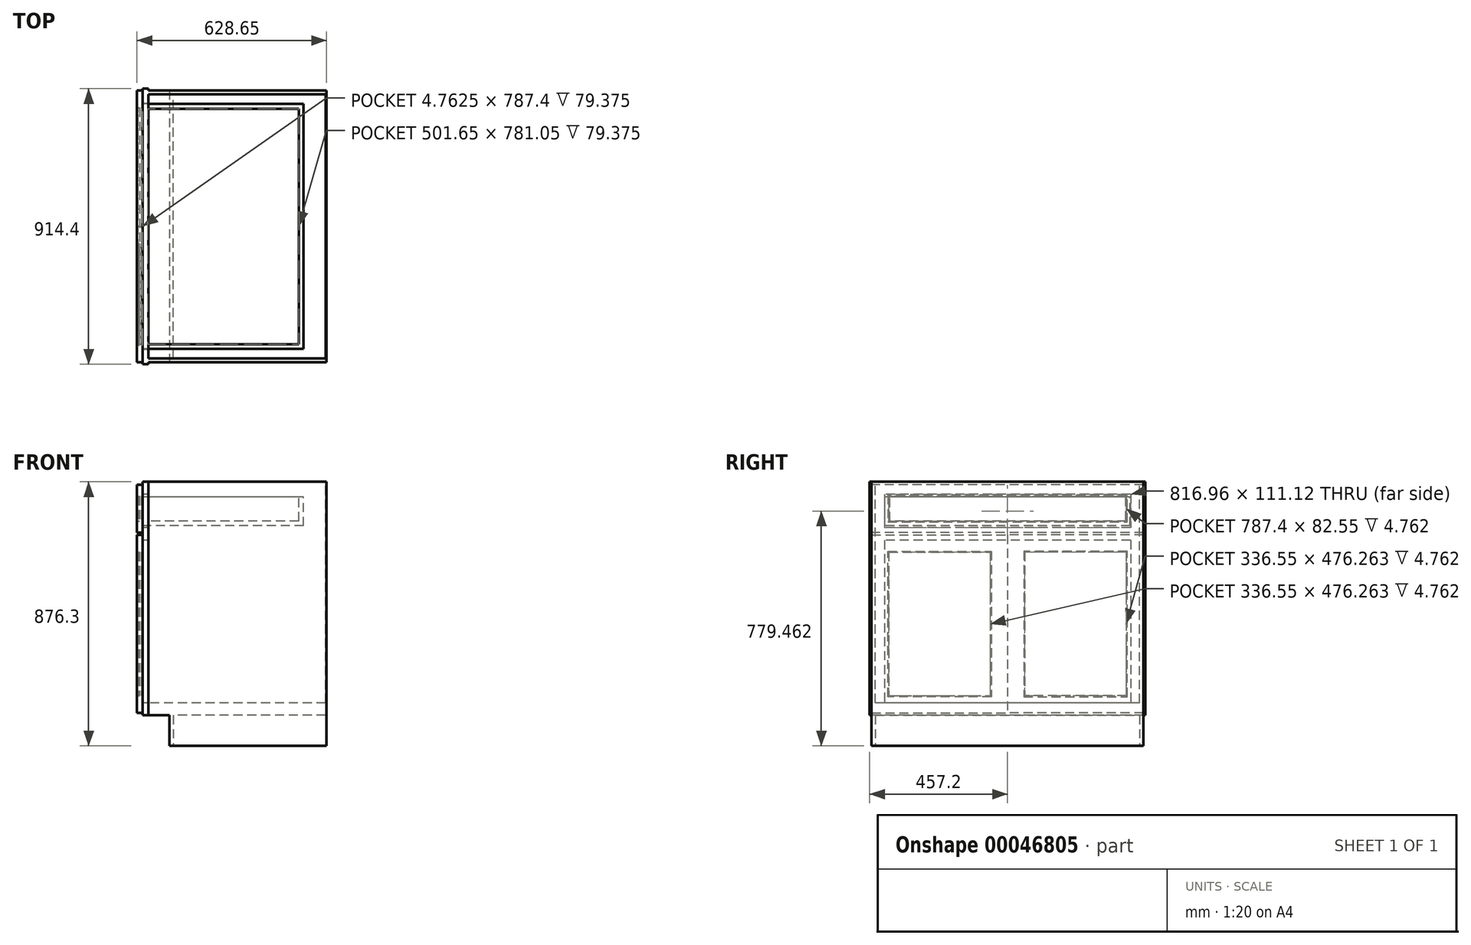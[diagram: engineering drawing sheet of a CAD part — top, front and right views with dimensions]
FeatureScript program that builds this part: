
annotation { "Feature Type Name" : "Feature", "Feature Type Description" : "" }
export const myFeature = defineFeature(function(context is Context, id is Id, definition is map)
    precondition{}
    {
        {
            var Q0;
            Q0=qCreatedBy(makeId("Front.planeOp"),FACE);
            var sketch = newSketch(context, id + "F0", { "sketchPlane" : qUnion([Q0])});
            skLineSegment(sketch, "E0.bottom", {"start": v(-304.8, -438.15) * mm, "end": v(304.8, -438.15) * mm});
            skLineSegment(sketch, "E0.top", {"start": v(-304.8, 438.15) * mm, "end": v(304.8, 438.15) * mm});
            skLineSegment(sketch, "E0.left", {"start": v(-304.8, -438.15) * mm, "end": v(-304.8, 438.15) * mm});
            skLineSegment(sketch, "E0.right", {"start": v(304.8, -438.15) * mm, "end": v(304.8, 438.15) * mm});
            skLineSegment(sketch, "E1", {"start": v(-304.8, -438.15) * mm, "end": v(304.8, 438.15) * mm, "construction": true});
            skSolve(sketch);
        }
        {
            var Q0;
            Q0=qSketchRegion(id+"F0",true);
            extrude(context, id + "F1", {"entities" : qUnion([Q0]), "oppositeDirection" : true, "depth" : 914.4 * mm});
        }
        {
            var Q0;
            Q0=makeQuery(id+"F1.opExtrude","CAP_FACE",FACE,{"disambiguationData":[OSD([sQuery(id+"F0.wireOp",EDGE,"E0.bottom"),sQuery(id+"F0.wireOp",EDGE,"E0.top"),sQuery(id+"F0.wireOp",EDGE,"E0.left"),sQuery(id+"F0.wireOp",EDGE,"E0.right")])],"isStart":true});
            var sketch = newSketch(context, id + "F2", { "sketchPlane" : qUnion([Q0])});
            skLineSegment(sketch, "E2.bottom", {"start": v(-304.8, -438.15) * mm, "end": v(-215.9, -438.15) * mm});
            skLineSegment(sketch, "E2.top", {"start": v(-304.8, -336.55) * mm, "end": v(-215.9, -336.55) * mm});
            skLineSegment(sketch, "E2.left", {"start": v(-304.8, -438.15) * mm, "end": v(-304.8, -336.55) * mm});
            skLineSegment(sketch, "E2.right", {"start": v(-215.9, -438.15) * mm, "end": v(-215.9, -336.55) * mm});
            skSolve(sketch);
        }
        {
            var Q0;
            Q0=qSketchRegion(id+"F2",true);
            extrude(context, id + "F3", {"entities" : qUnion([Q0]), "operationType" : NewBodyOperationType.REMOVE, "endBound" : BoundingType.THROUGH_ALL, "oppositeDirection" : true, "depth" : 25.4 * mm});
        }
        {
            var Q0;
            Q0=makeQuery(id+"F1.opExtrude","SWEPT_FACE",FACE,{"disambiguationData":[OSD([sQuery(id+"F0.wireOp",EDGE,"E0.left")])]});
            var sketch = newSketch(context, id + "F4", { "sketchPlane" : qUnion([Q0])});
            skLineSegment(sketch, "E3.bottom", {"start": v(-865.68, 396.88) * mm, "end": v(-48.72, 396.88) * mm});
            skLineSegment(sketch, "E3.top", {"start": v(-865.68, -295.28) * mm, "end": v(-48.72, -295.28) * mm});
            skLineSegment(sketch, "E3.left", {"start": v(-865.68, 396.88) * mm, "end": v(-865.68, -295.28) * mm});
            skLineSegment(sketch, "E3.right", {"start": v(-48.72, 396.88) * mm, "end": v(-48.72, -295.28) * mm});
            skLineSegment(sketch, "E4", {"start": v(-914.4, 438.15) * mm, "end": v(0, -336.55) * mm, "construction": true});
            skSolve(sketch);
        }
        {
            var Q0;
            Q0=qSketchRegion(id+"F4",true);
            extrude(context, id + "F5", {"entities" : qUnion([Q0]), "operationType" : NewBodyOperationType.REMOVE, "oppositeDirection" : true, "depth" : 19.05 * mm});
        }
        {
            var Q0;
            Q0=makeQuery(id+"F1.opExtrude","SWEPT_FACE",FACE,{"disambiguationData":[OSD([sQuery(id+"F0.wireOp",EDGE,"E0.top")])]});
            var sketch = newSketch(context, id + "F6", { "sketchPlane" : qUnion([Q0])});
            skLineSegment(sketch, "E5.bottom", {"start": v(304.8, 914.4) * mm, "end": v(-285.75, 914.4) * mm});
            skLineSegment(sketch, "E5.top", {"start": v(304.8, 908.05) * mm, "end": v(-285.75, 908.05) * mm});
            skLineSegment(sketch, "E5.left", {"start": v(304.8, 914.4) * mm, "end": v(304.8, 908.05) * mm});
            skLineSegment(sketch, "E5.right", {"start": v(-285.75, 914.4) * mm, "end": v(-285.75, 908.05) * mm});
            skLineSegment(sketch, "E6.bottom", {"start": v(304.8, 0) * mm, "end": v(-285.75, 0) * mm});
            skLineSegment(sketch, "E6.top", {"start": v(304.8, 6.35) * mm, "end": v(-285.75, 6.35) * mm});
            skLineSegment(sketch, "E6.left", {"start": v(304.8, 0) * mm, "end": v(304.8, 6.35) * mm});
            skLineSegment(sketch, "E6.right", {"start": v(-285.75, 0) * mm, "end": v(-285.75, 6.35) * mm});
            skSolve(sketch);
        }
        {
            var Q0;
            Q0=qSketchRegion(id+"F6",true);
            extrude(context, id + "F7", {"entities" : qUnion([Q0]), "operationType" : NewBodyOperationType.REMOVE, "endBound" : BoundingType.THROUGH_ALL, "oppositeDirection" : true, "depth" : 25.4 * mm});
        }
        {
            var Q0;
            Q0=makeQuery(id+"F1.opExtrude","SWEPT_FACE",FACE,{"disambiguationData":[OSD([sQuery(id+"F0.wireOp",EDGE,"E0.top")])]});
            var sketch = newSketch(context, id + "F8", { "sketchPlane" : qUnion([Q0])});
            skLineSegment(sketch, "E7.bottom", {"start": v(301.62, 895.35) * mm, "end": v(-285.75, 895.35) * mm});
            skLineSegment(sketch, "E7.top", {"start": v(301.63, 19.05) * mm, "end": v(-285.75, 19.05) * mm});
            skLineSegment(sketch, "E7.left", {"start": v(301.62, 895.35) * mm, "end": v(301.63, 19.05) * mm});
            skLineSegment(sketch, "E7.right", {"start": v(-285.75, 895.35) * mm, "end": v(-285.75, 19.05) * mm});
            skSolve(sketch);
        }
        {
            var Q0;
            Q0=qSketchRegion(id+"F8",true);
            var Q1;
            Q1=makeQuery(id+"F5.boolean.opBoolean","COPY",FACE,{"derivedFrom":makeQuery(id+"F5.opExtrude","SWEPT_FACE",FACE,{"disambiguationData":[OSD([sQuery(id+"F4.wireOp",EDGE,"E3.top")])]})});
            extrude(context, id + "F9", {"entities" : qUnion([Q0]), "operationType" : NewBodyOperationType.REMOVE, "endBound" : BoundingType.UP_TO_SURFACE, "oppositeDirection" : true, "endBoundEntityFace" : qUnion([Q1]), "depth" : 25.4 * mm});
        }
        {
            var Q0;
            Q0=makeQuery(id+"F1.opExtrude","SWEPT_FACE",FACE,{"disambiguationData":[OSD([sQuery(id+"F0.wireOp",EDGE,"E0.left")])]});
            var sketch = newSketch(context, id + "F10", { "sketchPlane" : qUnion([Q0])});
            skLineSegment(sketch, "E8.bottom", {"start": v(-865.68, 285.75) * mm, "end": v(-48.72, 285.75) * mm});
            skLineSegment(sketch, "E8.top", {"start": v(-865.68, 244.47) * mm, "end": v(-48.72, 244.47) * mm});
            skLineSegment(sketch, "E8.left", {"start": v(-865.68, 285.75) * mm, "end": v(-865.68, 244.47) * mm});
            skLineSegment(sketch, "E8.right", {"start": v(-48.72, 285.75) * mm, "end": v(-48.72, 244.47) * mm});
            skSolve(sketch);
        }
        {
            var Q0;
            Q0=qSketchRegion(id+"F10",true);
            var Q1;
            Q1=makeQuery(id+"F9.boolean.opBoolean","COPY",FACE,{"derivedFrom":makeQuery(id+"F9.opExtrude","SWEPT_FACE",FACE,{"disambiguationData":[OSD([sQuery(id+"F8.wireOp",EDGE,"E7.right")])]})});
            extrude(context, id + "F11", {"entities" : qUnion([Q0]), "operationType" : NewBodyOperationType.ADD, "endBound" : BoundingType.UP_TO_SURFACE, "oppositeDirection" : true, "endBoundEntityFace" : qUnion([Q1]), "depth" : 25.4 * mm});
        }
        {
            var Q0;
            Q0=makeQuery(id+"F11.boolean.opBoolean","MERGE",FACE,{"derivedFrom":[makeQuery(id+"F1.opExtrude","SWEPT_FACE",FACE,{"disambiguationData":[OSD([sQuery(id+"F0.wireOp",EDGE,"E0.left")])]}),makeQuery(id+"F11.opExtrude","CAP_FACE",FACE,{"disambiguationData":[OSD([sQuery(id+"F10.wireOp",EDGE,"E8.bottom"),sQuery(id+"F10.wireOp",EDGE,"E8.top"),sQuery(id+"F10.wireOp",EDGE,"E8.left"),sQuery(id+"F10.wireOp",EDGE,"E8.right")])],"isStart":true})]});
            var sketch = newSketch(context, id + "F12", { "sketchPlane" : qUnion([Q0])});
            skLineSegment(sketch, "E9.bottom", {"start": v(-908.05, 261.95) * mm, "end": v(-457.2, 261.95) * mm});
            skLineSegment(sketch, "E9.top", {"start": v(-908.05, -328.61) * mm, "end": v(-457.2, -328.61) * mm});
            skLineSegment(sketch, "E9.left", {"start": v(-908.05, 261.95) * mm, "end": v(-908.05, -328.61) * mm});
            skLineSegment(sketch, "E9.right", {"start": v(-457.2, 261.95) * mm, "end": v(-457.2, -328.61) * mm});
            skLineSegment(sketch, "E10.bottom", {"start": v(-850.9, 204.8) * mm, "end": v(-514.35, 204.8) * mm});
            skLineSegment(sketch, "E10.top", {"start": v(-850.9, -271.46) * mm, "end": v(-514.35, -271.46) * mm});
            skLineSegment(sketch, "E10.left", {"start": v(-850.9, 204.8) * mm, "end": v(-850.9, -271.46) * mm});
            skLineSegment(sketch, "E10.right", {"start": v(-514.35, 204.8) * mm, "end": v(-514.35, -271.46) * mm});
            skLineSegment(sketch, "E11", {"start": v(-457.2, 244.47) * mm, "end": v(-457.2, -295.28) * mm, "construction": true});
            skSolve(sketch);
        }
        {
            var Q0;
            Q0=qSketchRegion(id+"F12",true);
            extrude(context, id + "F13", {"entities" : qUnion([Q0]), "depth" : 19.05 * mm});
        }
        {
            var Q0;
            Q0=makeQuery(id+"F13.opExtrude","SWEPT_FACE",FACE,{"disambiguationData":[OSD([sQuery(id+"F12.wireOp",EDGE,"E10.top")])]});
            var sketch = newSketch(context, id + "F14", { "sketchPlane" : qUnion([Q0])});
            skLineSegment(sketch, "E12.bottom", {"start": v(-315.91, 850.9) * mm, "end": v(-309.56, 850.9) * mm});
            skLineSegment(sketch, "E12.top", {"start": v(-315.91, 514.35) * mm, "end": v(-309.56, 514.35) * mm});
            skLineSegment(sketch, "E12.left", {"start": v(-315.91, 850.9) * mm, "end": v(-315.91, 514.35) * mm});
            skLineSegment(sketch, "E12.right", {"start": v(-309.56, 850.9) * mm, "end": v(-309.56, 514.35) * mm});
            skSolve(sketch);
        }
        {
            var Q0;
            Q0=qSketchRegion(id+"F14",true);
            extrude(context, id + "F15", {"entities" : qUnion([Q0]), "operationType" : NewBodyOperationType.ADD, "endBound" : BoundingType.UP_TO_NEXT, "depth" : 25.4 * mm});
        }
        {
            var Q0;
            Q0=makeQuery(id+"F13.opExtrude","CAP_EDGE",EDGE,{"disambiguationData":[OSD([sQuery(id+"F12.wireOp",EDGE,"E10.left")])],"isStart":false});
            var Q1;
            Q1=makeQuery(id+"F13.opExtrude","CAP_EDGE",EDGE,{"disambiguationData":[OSD([sQuery(id+"F12.wireOp",EDGE,"E10.top")])],"isStart":false});
            var Q2;
            Q2=makeQuery(id+"F13.opExtrude","CAP_EDGE",EDGE,{"disambiguationData":[OSD([sQuery(id+"F12.wireOp",EDGE,"E10.right")])],"isStart":false});
            var Q3;
            Q3=makeQuery(id+"F13.opExtrude","CAP_EDGE",EDGE,{"disambiguationData":[OSD([sQuery(id+"F12.wireOp",EDGE,"E10.bottom")])],"isStart":false});
            chamfer(context, id + "F16", {"entities" : qUnion([Q0, Q1, Q2, Q3]), "width" : 3.17 * mm, "tangentPropagation" : true});
        }
        {
            var Q0;
            Q0=makeQuery(id+"F11.boolean.opBoolean","MERGE",FACE,{"derivedFrom":[makeQuery(id+"F1.opExtrude","SWEPT_FACE",FACE,{"disambiguationData":[OSD([sQuery(id+"F0.wireOp",EDGE,"E0.left")])]}),makeQuery(id+"F11.opExtrude","CAP_FACE",FACE,{"disambiguationData":[OSD([sQuery(id+"F10.wireOp",EDGE,"E8.bottom"),sQuery(id+"F10.wireOp",EDGE,"E8.top"),sQuery(id+"F10.wireOp",EDGE,"E8.left"),sQuery(id+"F10.wireOp",EDGE,"E8.right")])],"isStart":true})]});
            var sketch = newSketch(context, id + "F17", { "sketchPlane" : qUnion([Q0])});
            skLineSegment(sketch, "E13.bottom", {"start": v(-908.05, 428.62) * mm, "end": v(-6.35, 428.62) * mm});
            skLineSegment(sketch, "E13.top", {"start": v(-908.05, 269.88) * mm, "end": v(-6.35, 269.88) * mm});
            skLineSegment(sketch, "E13.left", {"start": v(-908.05, 428.62) * mm, "end": v(-908.05, 269.88) * mm});
            skLineSegment(sketch, "E13.right", {"start": v(-6.35, 428.63) * mm, "end": v(-6.35, 269.88) * mm});
            skLineSegment(sketch, "E14.bottom", {"start": v(-850.9, 390.52) * mm, "end": v(-63.5, 390.52) * mm});
            skLineSegment(sketch, "E14.top", {"start": v(-850.9, 307.98) * mm, "end": v(-63.5, 307.98) * mm});
            skLineSegment(sketch, "E14.left", {"start": v(-850.9, 390.52) * mm, "end": v(-850.9, 307.98) * mm});
            skLineSegment(sketch, "E14.right", {"start": v(-63.5, 390.53) * mm, "end": v(-63.5, 307.98) * mm});
            skSolve(sketch);
        }
        {
            var Q0;
            Q0=qSketchRegion(id+"F17",true);
            extrude(context, id + "F18", {"entities" : qUnion([Q0]), "depth" : 19.05 * mm});
        }
        {
            var Q0;
            Q0=makeQuery(id+"F18.opExtrude","SWEPT_FACE",FACE,{"disambiguationData":[OSD([sQuery(id+"F17.wireOp",EDGE,"E14.top")])]});
            var sketch = newSketch(context, id + "F19", { "sketchPlane" : qUnion([Q0])});
            skLineSegment(sketch, "E15.bottom", {"start": v(-309.56, 850.9) * mm, "end": v(-315.91, 850.9) * mm});
            skLineSegment(sketch, "E15.top", {"start": v(-309.56, 63.5) * mm, "end": v(-315.91, 63.5) * mm});
            skLineSegment(sketch, "E15.left", {"start": v(-309.56, 850.9) * mm, "end": v(-309.56, 63.5) * mm});
            skLineSegment(sketch, "E15.right", {"start": v(-315.91, 850.9) * mm, "end": v(-315.91, 63.5) * mm});
            skSolve(sketch);
        }
        {
            var Q0;
            Q0=qSketchRegion(id+"F19",true);
            var Q1;
            Q1=makeQuery(id+"F18.opExtrude","SWEPT_FACE",FACE,{"disambiguationData":[OSD([sQuery(id+"F17.wireOp",EDGE,"E14.bottom")])]});
            extrude(context, id + "F20", {"entities" : qUnion([Q0]), "operationType" : NewBodyOperationType.ADD, "endBound" : BoundingType.UP_TO_SURFACE, "endBoundEntityFace" : qUnion([Q1]), "depth" : 25.4 * mm});
        }
        {
            var Q0;
            Q0=makeQuery(id+"F18.opExtrude","CAP_EDGE",EDGE,{"disambiguationData":[OSD([sQuery(id+"F17.wireOp",EDGE,"E14.top")])],"isStart":false});
            var Q1;
            Q1=makeQuery(id+"F18.opExtrude","CAP_EDGE",EDGE,{"disambiguationData":[OSD([sQuery(id+"F17.wireOp",EDGE,"E14.left")])],"isStart":false});
            var Q2;
            Q2=makeQuery(id+"F18.opExtrude","CAP_EDGE",EDGE,{"disambiguationData":[OSD([sQuery(id+"F17.wireOp",EDGE,"E14.bottom")])],"isStart":false});
            var Q3;
            Q3=makeQuery(id+"F18.opExtrude","CAP_EDGE",EDGE,{"disambiguationData":[OSD([sQuery(id+"F17.wireOp",EDGE,"E14.right")])],"isStart":false});
            chamfer(context, id + "F21", {"entities" : qUnion([Q0, Q1, Q2, Q3]), "width" : 3.17 * mm, "tangentPropagation" : true});
        }
        {
            var Q0;
            Q0=makeQuery(id+"F1.opExtrude","SWEPT_FACE",FACE,{"disambiguationData":[OSD([sQuery(id+"F0.wireOp",EDGE,"E0.bottom")])]});
            var sketch = newSketch(context, id + "F22", { "sketchPlane" : qUnion([Q0])});
            skLineSegment(sketch, "E16.bottom", {"start": v(301.63, -19.05) * mm, "end": v(-203.2, -19.05) * mm});
            skLineSegment(sketch, "E16.top", {"start": v(301.63, -895.35) * mm, "end": v(-203.2, -895.35) * mm});
            skLineSegment(sketch, "E16.left", {"start": v(301.63, -19.05) * mm, "end": v(301.63, -895.35) * mm});
            skLineSegment(sketch, "E16.right", {"start": v(-203.2, -19.05) * mm, "end": v(-203.2, -895.35) * mm});
            skSolve(sketch);
        }
        {
            var Q0;
            Q0=qSketchRegion(id+"F22",true);
            extrude(context, id + "F23", {"entities" : qUnion([Q0]), "operationType" : NewBodyOperationType.REMOVE, "oppositeDirection" : true, "depth" : 101.6 * mm});
        }
        {
            var Q0;
            Q0=makeQuery(id+"F18.opExtrude","CAP_FACE",FACE,{"disambiguationData":[OSD([sQuery(id+"F17.wireOp",EDGE,"E13.bottom"),sQuery(id+"F17.wireOp",EDGE,"E13.top"),sQuery(id+"F17.wireOp",EDGE,"E13.left"),sQuery(id+"F17.wireOp",EDGE,"E13.right"),sQuery(id+"F17.wireOp",EDGE,"E14.bottom"),sQuery(id+"F17.wireOp",EDGE,"E14.top"),sQuery(id+"F17.wireOp",EDGE,"E14.left"),sQuery(id+"F17.wireOp",EDGE,"E14.right")])],"isStart":true});
            var sketch = newSketch(context, id + "F24", { "sketchPlane" : qUnion([Q0])});
            skLineSegment(sketch, "E17.bottom", {"start": v(863.6, 292.1) * mm, "end": v(50.8, 292.1) * mm});
            skLineSegment(sketch, "E17.top", {"start": v(863.6, 387.35) * mm, "end": v(50.8, 387.35) * mm});
            skLineSegment(sketch, "E17.left", {"start": v(863.6, 292.1) * mm, "end": v(863.6, 387.35) * mm});
            skLineSegment(sketch, "E17.right", {"start": v(50.8, 292.1) * mm, "end": v(50.8, 387.35) * mm});
            skSolve(sketch);
        }
        {
            var Q0;
            Q0=qSketchRegion(id+"F24",true);
            extrude(context, id + "F25", {"entities" : qUnion([Q0]), "operationType" : NewBodyOperationType.ADD, "depth" : 533.4 * mm});
        }
        {
            var Q0;
            Q0=makeQuery(id+"F25.opExtrude","SWEPT_FACE",FACE,{"disambiguationData":[OSD([sQuery(id+"F24.wireOp",EDGE,"E17.top")])]});
            shell(context, id + "F26", {"entities" : qUnion([Q0]), "thickness" : 15.88 * mm});
        }
        {
            var Q0;
            Q0=makeQuery(id+"F13.opExtrude","SWEPT_BODY",BODY,{"disambiguationData":[OSD([sQuery(id+"F12.wireOp",EDGE,"E9.bottom"),sQuery(id+"F12.wireOp",EDGE,"E9.top"),sQuery(id+"F12.wireOp",EDGE,"E9.left"),sQuery(id+"F12.wireOp",EDGE,"E9.right"),sQuery(id+"F12.wireOp",EDGE,"E10.bottom"),sQuery(id+"F12.wireOp",EDGE,"E10.top"),sQuery(id+"F12.wireOp",EDGE,"E10.left"),sQuery(id+"F12.wireOp",EDGE,"E10.right")])]});
            var Q1;
            Q1=makeQuery(id+"F13.opExtrude","SWEPT_FACE",FACE,{"disambiguationData":[OSD([sQuery(id+"F12.wireOp",EDGE,"E9.right")])]});
            mirror(context, id + "F27", {"entities" : qUnion([Q0]), "mirrorPlane" : qUnion([Q1])});
        }
    });
